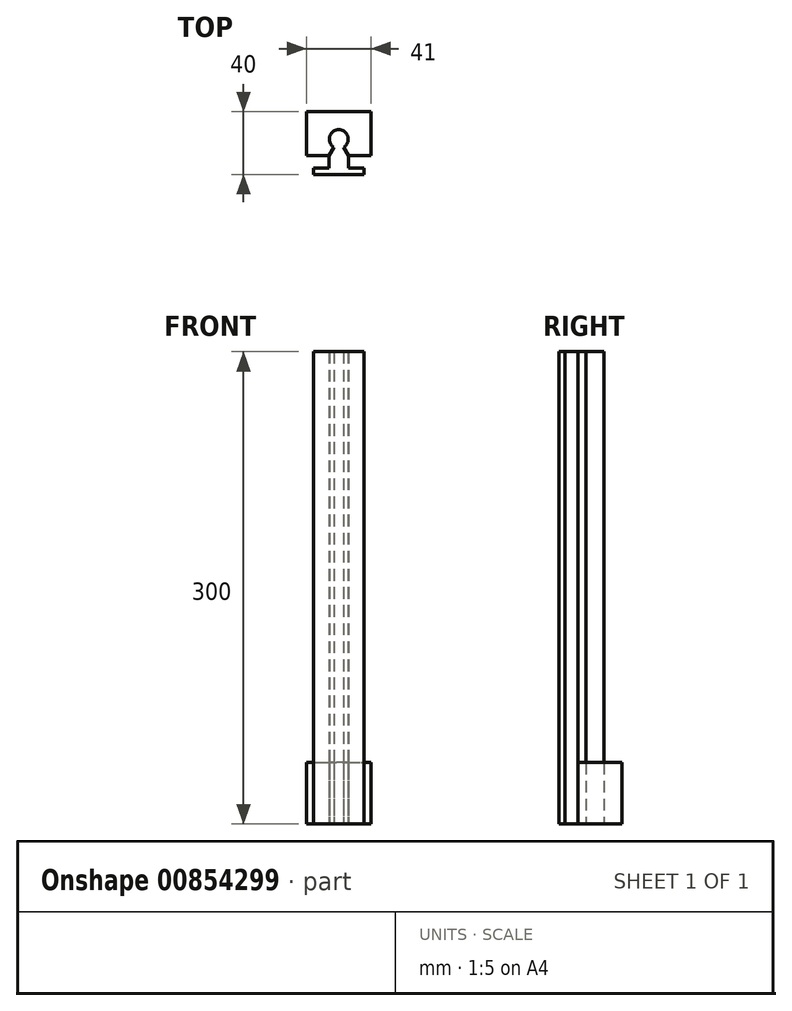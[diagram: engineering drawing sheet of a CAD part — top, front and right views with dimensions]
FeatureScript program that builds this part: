
annotation { "Feature Type Name" : "Feature", "Feature Type Description" : "" }
export const myFeature = defineFeature(function(context is Context, id is Id, definition is map)
    precondition{}
    {
        {
            var Q0;
            Q0=qCreatedBy(makeId("Top.planeOp"),FACE);
            var sketch = newSketch(context, id + "F0", { "sketchPlane" : qUnion([Q0])});
            skCircle(sketch, "E0", {"center": v(0, 22.5) * mm, "radius": 6 * mm});
            skLineSegment(sketch, "E1.bottom", {"start": v(-16, 4) * mm, "end": v(16, 4) * mm});
            skLineSegment(sketch, "E1.top", {"start": v(-16, 0) * mm, "end": v(16, 0) * mm});
            skLineSegment(sketch, "E1.left", {"start": v(-16, 4) * mm, "end": v(-16, 0) * mm});
            skLineSegment(sketch, "E1.right", {"start": v(16, 4) * mm, "end": v(16, 0) * mm});
            skLineSegment(sketch, "E2", {"start": v(0, 22.5) * mm, "end": v(0, 0) * mm, "construction": true});
            skPoint(sketch, "E3", {"position": v(-3, 17.3) * mm});
            skLineSegment(sketch, "E4", {"start": v(-3, 17.3) * mm, "end": v(-6.06, 12) * mm});
            skLineSegment(sketch, "E5", {"start": v(-6.06, 12) * mm, "end": v(-6.06, 4) * mm});
            skLineSegment(sketch, "E6.MirrorCS", {"start": v(3, 17.3) * mm, "end": v(6.06, 12) * mm});
            skLineSegment(sketch, "E7.MirrorCS", {"start": v(6.06, 12) * mm, "end": v(6.06, 4) * mm});
            skLineSegment(sketch, "E8", {"start": v(-20.5, 12) * mm, "end": v(-20.5, 40) * mm});
            skLineSegment(sketch, "E9", {"start": v(-20.5, 40) * mm, "end": v(20.5, 40) * mm});
            skLineSegment(sketch, "E10", {"start": v(20.5, 40) * mm, "end": v(20.5, 12) * mm});
            skLineSegment(sketch, "E11", {"start": v(0, 22.5) * mm, "end": v(0, 40) * mm, "construction": true});
            skLineSegment(sketch, "E12", {"start": v(-20.5, 12) * mm, "end": v(-6.06, 12) * mm});
            skLineSegment(sketch, "E13", {"start": v(6.06, 12) * mm, "end": v(20.5, 12) * mm});
            skSolve(sketch);
        }
        {
            var Q0;
            {var subQ0=sQuery(id+"F0.wireOp",EDGE,"E0");var subQ1=makeQuery(id+"F0.imprint","INTERSECT",VERTEX,{"derivedFrom":[subQ0,sQuery(id+"F0.wireOp",EDGE,"E4")]});Q0=makeQuery(id+"F0.imprint","IMPRINT",FACE,{"disambiguationData":[TD([[makeQuery(id+"F0.imprint","IMPRINT",EDGE,{"disambiguationData":[TD([[subQ1,-1.0]])],"derivedFrom":subQ0}),1.0]])]});}
            var Q1;
            {var subQ1=sQuery(id+"F0.wireOp",EDGE,"E4");Q1=makeQuery(id+"F0.imprint","IMPRINT",FACE,{"disambiguationData":[TD([[makeQuery(id+"F0.imprint","IMPRINT",EDGE,{"derivedFrom":subQ1}),1.0]])]});}
            var Q2;
            Q2=makeQuery(id+"F0.imprint","IMPRINT",FACE,{"disambiguationData":[TD([[makeQuery(id+"F0.imprint","IMPRINT",EDGE,{"derivedFrom":sQuery(id+"F0.wireOp",EDGE,"E1.top")}),1.0]])]});
            extrude(context, id + "F1", {"entities" : qUnion([Q0, Q1, Q2]), "depth" : 300 * mm, "offsetDistance" : 25 * mm});
        }
        {
            var Q0;
            {var subQ0=sQuery(id+"F0.wireOp",EDGE,"E4");Q0=makeQuery(id+"F0.imprint","IMPRINT",FACE,{"disambiguationData":[TD([[makeQuery(id+"F0.imprint","IMPRINT",EDGE,{"derivedFrom":subQ0}),-1.0]])]});}
            extrude(context, id + "F2", {"entities" : qUnion([Q0]), "depth" : 39 * mm, "offsetDistance" : 25 * mm});
        }
    });
